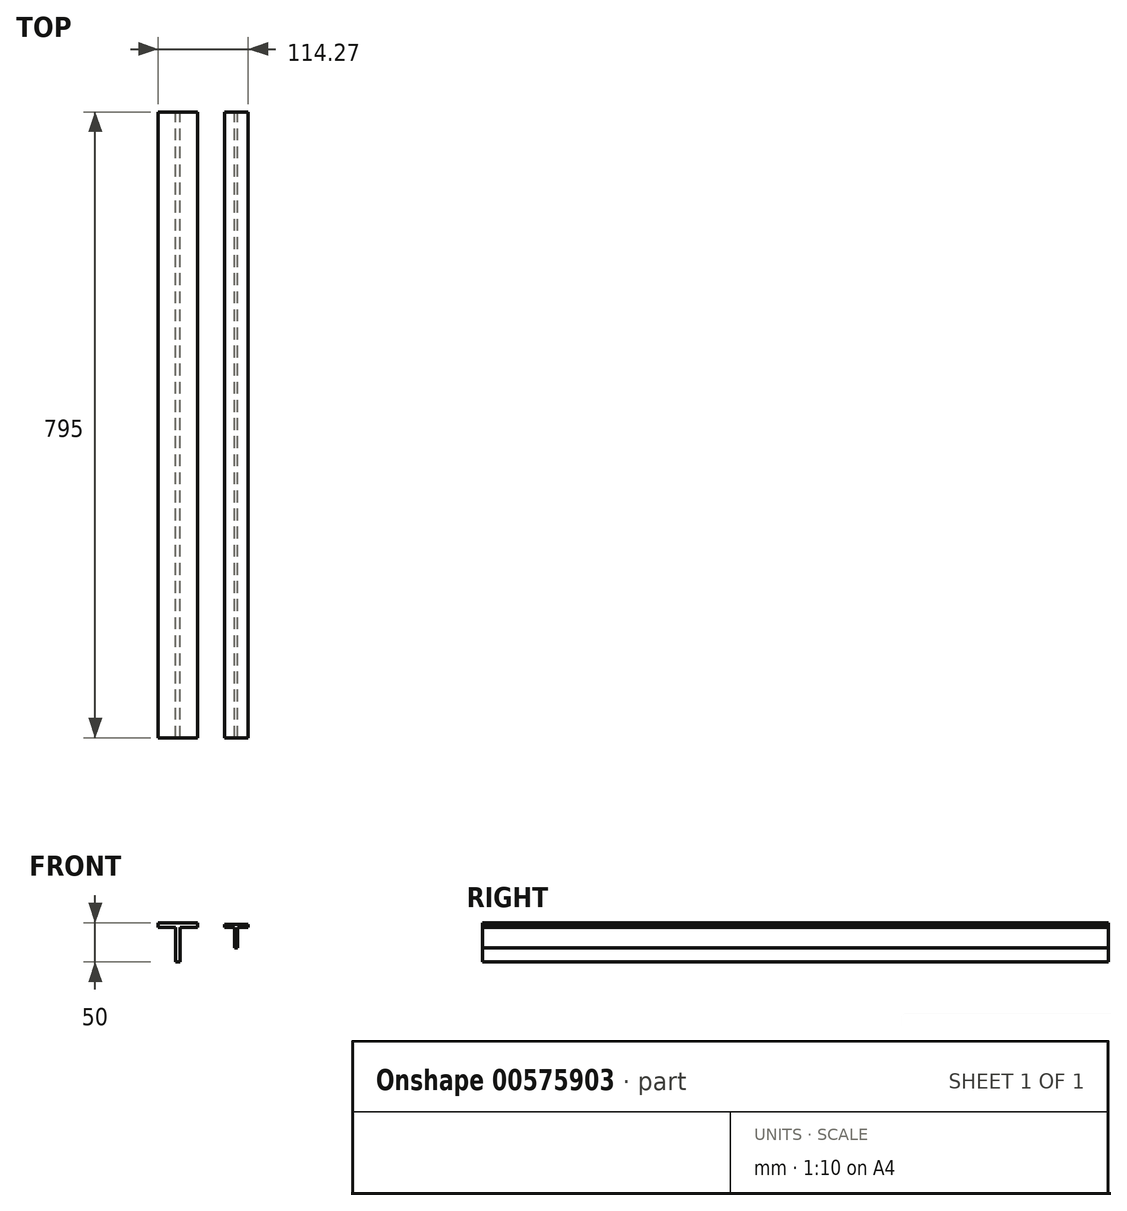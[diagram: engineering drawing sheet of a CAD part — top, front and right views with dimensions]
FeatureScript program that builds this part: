
annotation { "Feature Type Name" : "Feature", "Feature Type Description" : "" }
export const myFeature = defineFeature(function(context is Context, id is Id, definition is map)
    precondition{}
    {
        {
            var Q0;
            Q0=qCreatedBy(makeId("Front.planeOp"),FACE);
            var sketch = newSketch(context, id + "F0", { "sketchPlane" : qUnion([Q0])});
            skLineSegment(sketch, "E0.top", {"start": v(-51.15, -12.93) * mm, "end": v(-45.15, -12.93) * mm});
            skLineSegment(sketch, "E0.left", {"start": v(-51.15, 31.07) * mm, "end": v(-51.15, -12.93) * mm});
            skLineSegment(sketch, "E0.right", {"start": v(-45.15, 31.07) * mm, "end": v(-45.15, -12.93) * mm});
            skLineSegment(sketch, "E1.bottom", {"start": v(-72.97, 37.07) * mm, "end": v(-22.97, 37.07) * mm});
            skLineSegment(sketch, "E1.top", {"start": v(-72.97, 31.07) * mm, "end": v(-51.15, 31.07) * mm});
            skLineSegment(sketch, "E1.left", {"start": v(-72.97, 37.07) * mm, "end": v(-72.97, 31.07) * mm});
            skLineSegment(sketch, "E1.right", {"start": v(-22.97, 37.07) * mm, "end": v(-22.97, 31.07) * mm});
            skLineSegment(sketch, "E2.trimOffspring", {"start": v(-45.15, 31.07) * mm, "end": v(-22.97, 31.07) * mm});
            skPoint(sketch, "E3.firstSnap0", {"position": v(-62.06, 31.07) * mm});
            skLineSegment(sketch, "E3.bottom", {"start": v(11.3, 31.07) * mm, "end": v(23.75, 31.07) * mm});
            skLineSegment(sketch, "E3.top", {"start": v(11.3, 35.07) * mm, "end": v(41.3, 35.07) * mm});
            skLineSegment(sketch, "E3.left", {"start": v(11.3, 31.07) * mm, "end": v(11.3, 35.07) * mm});
            skLineSegment(sketch, "E3.right", {"start": v(41.3, 31.07) * mm, "end": v(41.3, 35.07) * mm});
            skLineSegment(sketch, "E4.bottom", {"start": v(23.75, 5.07) * mm, "end": v(27.75, 5.07) * mm});
            skLineSegment(sketch, "E4.left", {"start": v(23.75, 5.07) * mm, "end": v(23.75, 31.07) * mm});
            skLineSegment(sketch, "E4.right", {"start": v(27.75, 5.07) * mm, "end": v(27.75, 31.07) * mm});
            skLineSegment(sketch, "E5.trimOffspring", {"start": v(27.75, 31.07) * mm, "end": v(41.3, 31.07) * mm});
            skSolve(sketch);
        }
        {
            var Q0;
            Q0=makeQuery(id+"F0.imprint","IMPRINT",FACE,{"disambiguationData":[TD([[makeQuery(id+"F0.imprint","IMPRINT",EDGE,{"derivedFrom":sQuery(id+"F0.wireOp",EDGE,"E0.top")}),1.0]])]});
            extrude(context, id + "F1", {"entities" : qUnion([Q0]), "depth" : 795 * mm, "offsetDistance" : 25 * mm});
        }
        {
            var Q0;
            Q0=makeQuery(id+"F0.imprint","IMPRINT",FACE,{"disambiguationData":[TD([[makeQuery(id+"F0.imprint","IMPRINT",EDGE,{"derivedFrom":sQuery(id+"F0.wireOp",EDGE,"E3.bottom")}),1.0]])]});
            extrude(context, id + "F2", {"entities" : qUnion([Q0]), "depth" : 795 * mm, "offsetDistance" : 25 * mm});
        }
    });
